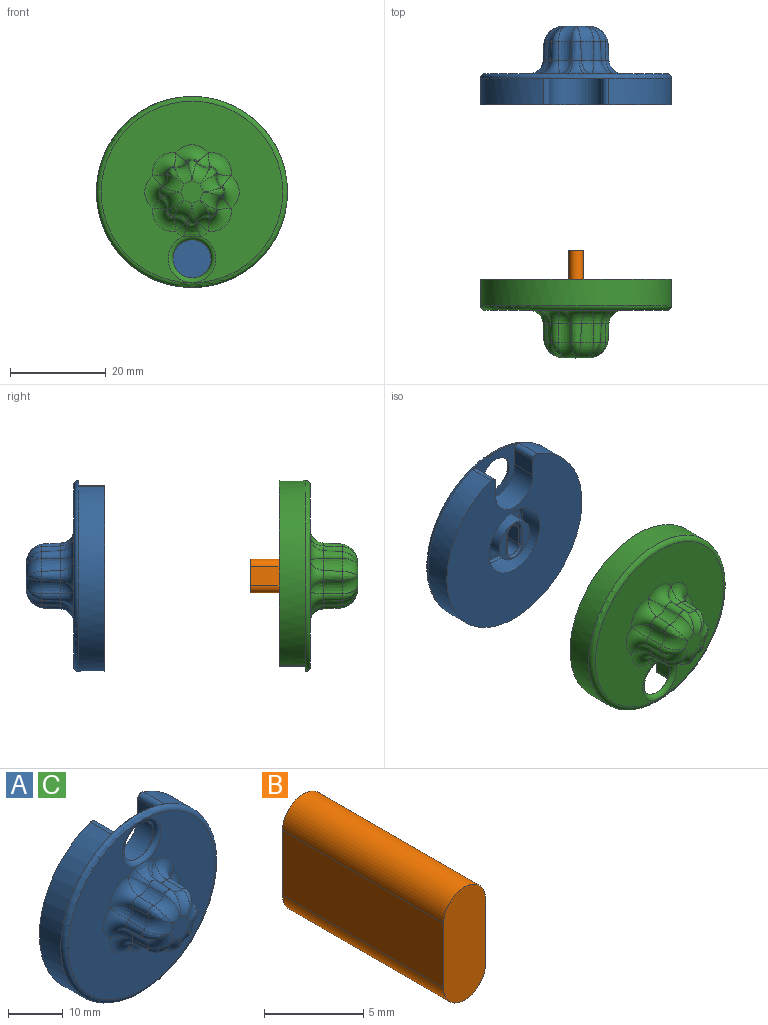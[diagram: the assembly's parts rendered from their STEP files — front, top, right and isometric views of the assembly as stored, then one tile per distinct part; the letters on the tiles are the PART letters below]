
ASSEMBLY  parts=3 mates=2
PART A: 79 faces, bbox 43.3x16.5x43.3 mm
  f0: plane 38.02x38.02mm, normal (0,-1,0), area 771.7mm2, adj f1,f26,f70,f71,f72,f73,f74,f75
  f1: torus R=19.01mm, axis (0,-1,0), area 191.9mm2, adj f0,f2
  f2: cylinder r=20mm len=40mm, axis (0,1,0), area 615.8mm2, adj f1,f3,f8,f9,f25
  f3: plane 13.66x11.5mm, normal (0,1,0), area 61.3mm2, adj f2,f4,f5,f6,f7,f8,f25
  f4: plane 5.5x3.87mm, normal (1,0,0), area 21.3mm2, adj f3,f5,f9,f25
  f5: cylinder r=5.5mm len=11mm, axis (0,1,0), area 95mm2, adj f3,f4,f6,f9
  f6: plane 5.5x3.87mm, normal (-1,0,0), area 21.3mm2, adj f3,f5,f8,f9
  f7: cylinder r=4mm len=8mm, axis (0,1,0), area 0.3mm2, adj f3,f78
  f8: cylinder r=0.99mm len=5.5mm, axis (0,1,0), area 10.5mm2, adj f2,f3,f6,f9
  f9: plane 40x38.86mm, normal (0,1,0), area 968.3mm2, adj f2,f4,f5,f6,f8,f10,f25
  f10: cylinder r=7.5mm len=15mm, axis (0,1,0), area 235.6mm2, adj f9,f11
  f11: torus R=7mm, axis (0,1,0), area 36.1mm2, adj f10,f12
  f12: plane 14x14mm, normal (0,1,0), area 75.4mm2, adj f11,f13
  f13: torus R=5mm, axis (0,1,0), area 23.1mm2, adj f12,f14
  f14: cylinder r=4.5mm len=9mm, axis (0,1,0), area 141.4mm2, adj f13,f15
  f15: plane 9x9mm, normal (0,1,0), area 28.6mm2, adj f14,f16,f22,f23,f24
  f16: torus R=2.3mm, axis (0,-1,0), area 4.9mm2, adj f15,f17,f22,f24
  f17: cylinder r=1.8mm len=5mm, axis (0,1,0), area 28.3mm2, adj f16,f18,f20,f21
  f18: plane 5x4mm, normal (1,0,0), area 20mm2, adj f17,f19,f21,f24
  f19: cylinder r=1.8mm len=5mm, axis (0,1,0), area 28.3mm2, adj f18,f20,f21,f23
  f20: plane 5x4mm, normal (-1,0,0), area 20mm2, adj f17,f19,f21,f22
  f21: plane 7.6x3.6mm, normal (0,1,0), area 24.6mm2, adj f17,f18,f19,f20
  f22: cylinder r=0.5mm len=4mm, axis (0,0,-1), area 3.1mm2, adj f15,f16,f20,f23
  f23: torus R=2.3mm, axis (0,-1,0), area 4.9mm2, adj f15,f19,f22,f24
  f24: cylinder r=0.5mm len=4mm, axis (0,0,1), area 3.1mm2, adj f15,f16,f18,f23
  f25: cylinder r=0.99mm len=5.5mm, axis (0,1,0), area 10.5mm2, adj f2,f3,f4,f9
  f26: torus R=4.39mm, axis (0,-1,0), area 5.2mm2, adj f0,f27,f68,f69
  f27: bspline ~3.03x2.86mm, area 5.2mm2, adj f26,f28,f70
  f28: cone r=2.36mm half-angle=3deg, axis (0,-1,0), area 11.4mm2, adj f27,f29,f67,f68
  f29: cone r=1.55mm half-angle=3deg, axis (0,1,0), area 9.6mm2, adj f28,f30,f65,f70
  f30: bspline ~3.38x3.37mm, area 4.6mm2, adj f29,f31,f67
  f31: torus R=6.21mm, axis (0,-1,0), area 14mm2, adj f30,f32,f64,f65
  f32: plane 4.83x4.83mm, normal (0,-1,0), area 15.8mm2, adj f31,f33,f58,f59,f61,f62,f63,f67
  f33: torus R=6.21mm, axis (0,-1,0), area 14mm2, adj f32,f34,f50,f51,f57
  f34: bspline ~3.02x2.67mm, area 3.8mm2, adj f33,f35,f63
  f35: cone r=1.55mm half-angle=3deg, axis (0,1,0), area 9.6mm2, adj f34,f36,f51,f73
  f36: cone r=2.36mm half-angle=3deg, axis (0,-1,0), area 11.4mm2, adj f35,f37,f38,f63
  f37: bspline ~3.03x2.86mm, area 5.2mm2, adj f36,f73,f74
  f38: cone r=1.55mm half-angle=3deg, axis (0,1,0), area 9.6mm2, adj f36,f39,f40,f74
  f39: bspline ~3.38x3.37mm, area 4.6mm2, adj f38,f62,f63
  f40: cone r=2.36mm half-angle=3deg, axis (0,-1,0), area 11.4mm2, adj f38,f41,f42,f62
  f41: bspline ~3.03x2.86mm, area 5.2mm2, adj f40,f74,f75
  f42: cone r=1.55mm half-angle=3deg, axis (0,1,0), area 9.6mm2, adj f40,f43,f44,f75
  f43: bspline ~4.27x3.32mm, area 5.5mm2, adj f42,f61,f62
  f44: cone r=2.36mm half-angle=3deg, axis (0,-1,0), area 11.4mm2, adj f42,f45,f46,f61
  f45: bspline ~3.03x2.86mm, area 5.2mm2, adj f44,f75,f76
  f46: cone r=1.55mm half-angle=3deg, axis (0,1,0), area 9.6mm2, adj f44,f47,f48,f76
  f47: bspline ~3.38x3.37mm, area 4.6mm2, adj f46,f59,f61
  f48: cone r=2.36mm half-angle=3deg, axis (0,-1,0), area 11.4mm2, adj f46,f49,f59,f68
  f49: bspline ~3.03x2.86mm, area 5.2mm2, adj f48,f76,f77
  f50: bspline ~2.03x0.58mm, area 0.1mm2, adj f33,f63
  f51: cone r=2.36mm half-angle=3deg, axis (0,-1,0), area 11.4mm2, adj f33,f35,f52,f56
  f52: cone r=1.55mm half-angle=3deg, axis (0,1,0), area 9.6mm2, adj f51,f53,f57,f72
  f53: cone r=2.36mm half-angle=3deg, axis (0,-1,0), area 11.4mm2, adj f52,f54,f55,f58
  f54: cone r=1.55mm half-angle=3deg, axis (0,1,0), area 9.6mm2, adj f53,f64,f65,f71
  f55: bspline ~3.03x2.86mm, area 5.2mm2, adj f53,f71,f72
  f56: bspline ~3.03x2.86mm, area 5.2mm2, adj f51,f72,f73
  f57: bspline ~3.38x3.37mm, area 4.6mm2, adj f33,f52,f58
  f58: torus R=6.21mm, axis (0,-1,0), area 14mm2, adj f32,f53,f57,f64
  f59: torus R=6.21mm, axis (0,-1,0), area 14mm2, adj f32,f47,f48,f60
  f60: bspline ~4.27x3.32mm, area 5.4mm2, adj f59,f67,f68
  f61: torus R=6.21mm, axis (0,-1,0), area 14mm2, adj f32,f43,f44,f47
  f62: torus R=6.21mm, axis (0,-1,0), area 14mm2, adj f32,f39,f40,f43
  f63: torus R=6.21mm, axis (0,-1,0), area 14mm2, adj f32,f34,f36,f39,f50
  f64: bspline ~4.27x3.32mm, area 5.2mm2, adj f31,f54,f58
  f65: cone r=2.36mm half-angle=3deg, axis (0,-1,0), area 11.4mm2, adj f29,f31,f54,f66
  f66: bspline ~3.03x2.86mm, area 5.2mm2, adj f65,f70,f71
  f67: torus R=6.21mm, axis (0,-1,0), area 14mm2, adj f28,f30,f32,f60
  f68: cone r=1.55mm half-angle=3deg, axis (0,1,0), area 9.6mm2, adj f26,f28,f48,f60,f69,f77
  f69: bspline ~4.88x3.08mm, area 9mm2, adj f26,f68,f77,f78
  f70: torus R=4.39mm, axis (0,-1,0), area 21.1mm2, adj f0,f27,f29,f66
  f71: torus R=4.39mm, axis (0,-1,0), area 21.1mm2, adj f0,f54,f55,f66
  f72: torus R=4.39mm, axis (0,-1,0), area 21.1mm2, adj f0,f52,f55,f56
  f73: torus R=4.39mm, axis (0,-1,0), area 21.1mm2, adj f0,f35,f37,f56
  f74: torus R=4.39mm, axis (0,-1,0), area 21.1mm2, adj f0,f37,f38,f41
  f75: torus R=4.39mm, axis (0,-1,0), area 21.1mm2, adj f0,f41,f42,f45
  f76: torus R=4.39mm, axis (0,-1,0), area 21.1mm2, adj f0,f45,f46,f49
  f77: torus R=4.39mm, axis (0,-1,0), area 5.2mm2, adj f0,f49,f68,f69
  f78: torus R=4.99mm, axis (0,-1,0), area 42.2mm2, adj f0,f7,f69
PART B: 6 faces, bbox 3x11.5x7 mm
  f0: plane 7x3mm, normal (0,-1,0), area 19.1mm2, adj f1,f2,f3,f4
  f1: plane 11.5x4mm, normal (-1,0,0), area 46mm2, adj f0,f2,f3,f5
  f2: cylinder r=1.5mm len=11.5mm, axis (0,1,0), area 54.2mm2, adj f0,f1,f4,f5
  f3: cylinder r=1.5mm len=11.5mm, axis (0,1,0), area 54.2mm2, adj f0,f1,f4,f5
  f4: plane 11.5x4mm, normal (1,0,0), area 46mm2, adj f0,f2,f3,f5
  f5: plane 7x3mm, normal (0,1,0), area 19.1mm2, adj f1,f2,f3,f4
PART C: same geometry as A
PLACE A rot(axis=(0,0,1),180deg) t=(0,3.02,157.22)mm
PLACE B rot(axis=(0,-1,0),180deg) t=(0,-33.99,157.22)mm
PLACE C rot(axis=(0,1,0),180deg) t=(0,-33.49,157.22)mm
MATE slider B.f5 <-> A.f1  axis (0,1,0) through (0,-27.49,157.22)mm
MATE fastened B.f0 <-> C.f1  axis (0,-1,0) through (0,-38.99,157.22)mm
